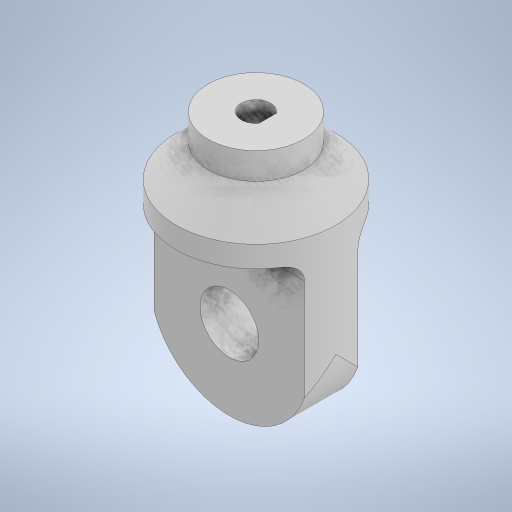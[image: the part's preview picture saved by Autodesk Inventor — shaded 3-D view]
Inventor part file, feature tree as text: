
AUTODESK INVENTOR PART (.ipt)
format: ipt  version: 2023 (Build 270158000, 158)  size: 356,352 bytes
history: native  units: mm
features: sketch x7, extrude x6, projected_geometry x2, other x1, chamfer x1, fillet x1, revolve x1, pattern_circular x1
ambient origin geometry x8: Origin, YZ Plane, XZ Plane, XY Plane, X Axis, Y Axis, Z Axis, Center Point
bodies: Body1 (feature_tree)
feature tree (20):
  other  "솔리드1"
  extrude  "돌출1"  Depth=30.0mm
  extrude  "돌출2"  Depth=10.0mm TaperAngle=0.0deg
  extrude  "돌출3"  Depth=10.0mm
  chamfer  "모따기1"  Distance=32.0mm
  fillet  "모깎기1"  Radius=30.0mm
  revolve  "회전1"
  extrude  "돌출4"  Depth=32.0mm TaperAngle=0.0deg
  pattern_circular  "원형 패턴1"  Angle=45.0deg  [1 undecoded]
  extrude  "돌출5"  Depth=3.0mm
  extrude  "돌출6"  Depth=30.0mm
  sketch  "스케치1"
  sketch  "스케치2"
  projected_geometry  "투영된 루프1"
  sketch  "스케치3"
  sketch  "스케치4"
  sketch  "스케치5"
  sketch  "스케치6"
  projected_geometry  "투영된 루프2"
  sketch  "스케치7"
note: 1 required parameter value undecoded (feature->parameter linkage not recoverable at this tier; creation-order binding heuristic only, values carry confidence <= 0.55)
